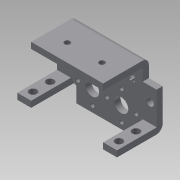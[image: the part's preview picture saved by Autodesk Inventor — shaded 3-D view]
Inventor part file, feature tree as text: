
AUTODESK INVENTOR PART (.ipt)
format: ipt  version: 2015 SP1 (Build 190203100, 203)  size: 495,104 bytes
history: native  units: mm
features: sketch x19, extrude x18, reference x11, projected_geometry x7, fillet x3, mirror x3
ambient origin geometry x8: Origin, YZ Plane, XZ Plane, XY Plane, X Axis, Y Axis, Z Axis, Center Point
bodies: Solid1 (feature_tree)
feature tree (61):
  extrude  "Extrusion1"  Depth=29.21mm
  extrude  "Extrusion2"  Depth=3.5mm
  extrude  "Extrusion3"  Depth=57.15mm TaperAngle=0.0deg
  sketch  "Sketch5"  dims[d8=57.15mm d9=0.0mm d11=25.147mm d12=0.0mm d13=0.254mm]
  extrude  "Extrusion4"  Depth=0.254mm TaperAngle=0.0deg
  fillet  "Fillet1"  Radius=0.254mm
  extrude  "Extrusion5"  Depth=3.75mm
  mirror  "Mirror1"
  fillet  "Fillet2"  Radius=22.4282mm
  extrude  "Extrusion6"  Depth=25.147mm TaperAngle=0.0deg
  extrude  "Extrusion7"  Depth=3.5mm TaperAngle=0.0deg
  extrude  "Extrusion8"  Depth=3.5mm TaperAngle=0.0deg
  extrude  "Extrusion9"  Depth=22.682mm TaperAngle=0.0deg
  extrude  "Extrusion10"  Depth=7.95mm TaperAngle=0.0deg
  sketch  "Sketch16"  dims[d38=7.95mm d39=0.0mm d43=7.95mm d44=0.0mm d47=3.5mm d48=0.0mm]
  extrude  "Extrusion11"  Depth=7.95mm TaperAngle=0.0deg
  fillet  "Fillet3"  Radius=3.5mm
  sketch  "Sketch19"  dims[d50=2.0mm d51=3.5mm d52=0.0mm]
  extrude  "Extrusion12"  Depth=3.5mm TaperAngle=0.0deg
  mirror  "Mirror2"
  extrude  "Extrusion13"  Depth=3.5mm TaperAngle=0.0deg
  extrude  "Extrusion15"  [1 undecoded]
  sketch  "Sketch24"
  sketch  "Sketch25"
  extrude  "Extrusion17"  [1 undecoded]
  extrude  "Extrusion18"  [1 undecoded]
  mirror  "Mirror4"
  extrude  "Extrusion19"  [1 undecoded]
  extrude  "Extrusion20"  [1 undecoded]
  sketch  "Sketch1"  dims[d0=57.15mm d1=29.21mm]
  sketch  "Sketch2"  dims[d2=3.5mm d3=0.0mm d4=3.5mm]
  sketch  "Sketch4"  dims[d5=3.5mm d6=57.15mm d7=0.0mm]
  sketch  "Sketch9"  dims[d15=25.147mm d16=0.0mm d17=3.75mm d18=22.4282mm]
  reference  "Reference3"
  reference  "Reference4"
  sketch  "Sketch11"  dims[d19=22.428mm d20=25.147mm d21=0.0mm]
  reference  "Reference7"
  sketch  "Sketch12"  dims[d22=25.147mm d23=0.0mm d24=3.5mm d25=0.0mm]
  reference  "Reference8"
  reference  "Reference9"
  sketch  "Sketch13"  dims[d26=3.5mm d27=0.0mm d28=3.5mm d29=0.0mm]
  sketch  "Sketch14"  dims[d30=3.5mm d33=22.682mm d34=0.0mm]
  sketch  "Sketch15"  dims[d35=0.254mm d36=7.95mm d37=0.0mm]
  reference  "Reference24"
  projected_geometry  "Projected Loop1"
  sketch  "Sketch21"  dims[d53=3.5mm d54=0.0mm d55=3.5mm d56=0.0mm]
  projected_geometry  "Projected Loop2"
  sketch  "Sketch23"
  reference  "Reference26"
  reference  "Reference27"
  reference  "Reference28"
  reference  "Reference29"
  reference  "Reference30"
  sketch  "Sketch26"
  sketch  "Sketch27"
  sketch  "Sketch28"
  projected_geometry  "Projected Loop3"
  projected_geometry  "Projected Loop4"
  projected_geometry  "Projected Loop5"
  projected_geometry  "Projected Loop6"
  projected_geometry  "Projected Loop7"
note: 5 required parameter values undecoded (feature->parameter linkage not recoverable at this tier; creation-order binding heuristic only, values carry confidence <= 0.55)
